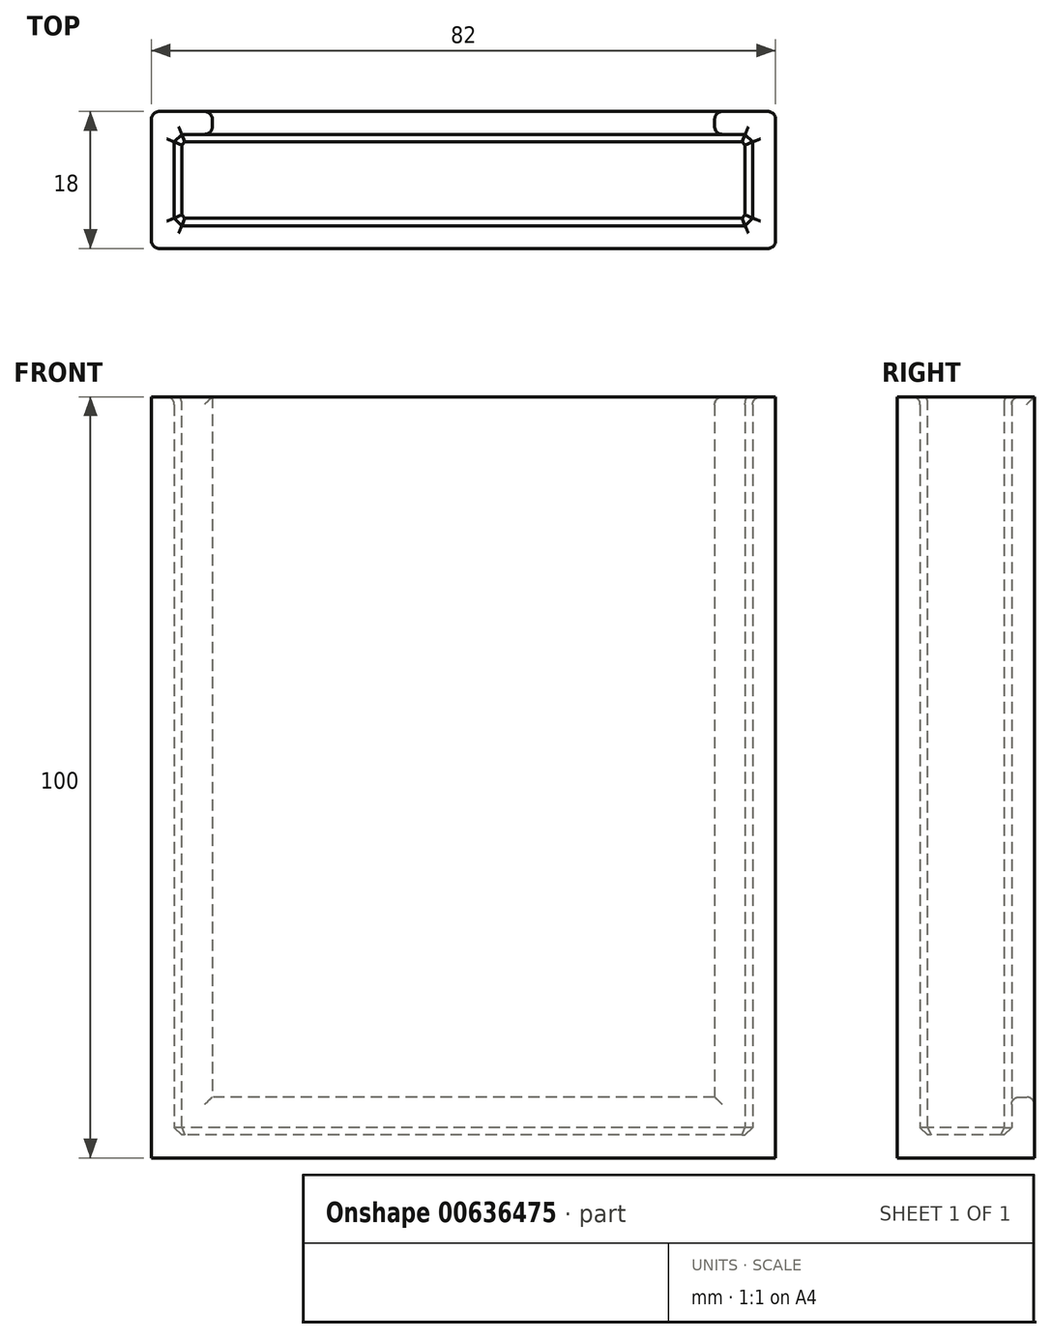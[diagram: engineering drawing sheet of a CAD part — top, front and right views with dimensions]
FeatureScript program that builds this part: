
annotation { "Feature Type Name" : "Feature", "Feature Type Description" : "" }
export const myFeature = defineFeature(function(context is Context, id is Id, definition is map)
    precondition{}
    {
        {
            var Q0;
            Q0=qCreatedBy(makeId("Top.planeOp"),FACE);
            var sketch = newSketch(context, id + "F0", { "sketchPlane" : qUnion([Q0])});
            skLineSegment(sketch, "E0", {"start": v(0, 10.86) * mm, "end": v(-38, 10.86) * mm});
            skLineSegment(sketch, "E1", {"start": v(0, 10.86) * mm, "end": v(38, 10.86) * mm});
            skLineSegment(sketch, "E2", {"start": v(-38, 10.86) * mm, "end": v(-38, 22.86) * mm});
            skLineSegment(sketch, "E3", {"start": v(-38, 22.86) * mm, "end": v(-33, 22.86) * mm});
            skLineSegment(sketch, "E4", {"start": v(-33, 22.86) * mm, "end": v(-33, 25.86) * mm});
            skLineSegment(sketch, "E5", {"start": v(-33, 25.86) * mm, "end": v(-41, 25.86) * mm});
            skLineSegment(sketch, "E6", {"start": v(-41, 25.86) * mm, "end": v(-41, 7.86) * mm});
            skLineSegment(sketch, "E7", {"start": v(-41, 7.86) * mm, "end": v(0, 7.86) * mm});
            skLineSegment(sketch, "E8", {"start": v(0, 7.86) * mm, "end": v(41, 7.86) * mm});
            skLineSegment(sketch, "E9", {"start": v(41, 7.86) * mm, "end": v(41, 25.86) * mm});
            skLineSegment(sketch, "E10", {"start": v(41, 25.86) * mm, "end": v(33, 25.86) * mm});
            skLineSegment(sketch, "E11", {"start": v(33, 25.86) * mm, "end": v(33, 22.86) * mm});
            skLineSegment(sketch, "E12", {"start": v(33, 22.86) * mm, "end": v(38, 22.86) * mm});
            skLineSegment(sketch, "E13", {"start": v(38, 22.86) * mm, "end": v(38, 10.86) * mm});
            skLineSegment(sketch, "E14", {"start": v(41, 25.86) * mm, "end": v(-41, 25.86) * mm});
            skLineSegment(sketch, "E15", {"start": v(33, 22.86) * mm, "end": v(-33, 22.86) * mm});
            skSolve(sketch);
        }
        {
            var Q0;
            Q0=makeQuery(id+"F0.imprint","IMPRINT",FACE,{"disambiguationData":[TD([[makeQuery(id+"F0.imprint","IMPRINT",EDGE,{"derivedFrom":sQuery(id+"F0.wireOp",EDGE,"E0")}),1.0]])]});
            extrude(context, id + "F1", {"entities" : qUnion([Q0]), "depth" : 100 * mm, "offsetDistance" : 25 * mm});
        }
        {
            var Q0;
            Q0=makeQuery(id+"F1.opExtrude","SWEPT_EDGE",EDGE,{"disambiguationData":[OSD([sQuery(id+"F0.wireOp",EDGE,"E9"),sQuery(id+"F0.wireOp",EDGE,"E14")])]});
            var Q1;
            Q1=makeQuery(id+"F1.opExtrude","SWEPT_EDGE",EDGE,{"disambiguationData":[OSD([sQuery(id+"F0.wireOp",EDGE,"E8"),sQuery(id+"F0.wireOp",EDGE,"E9")])]});
            var Q2;
            Q2=makeQuery(id+"F1.opExtrude","SWEPT_EDGE",EDGE,{"disambiguationData":[OSD([sQuery(id+"F0.wireOp",EDGE,"E6"),sQuery(id+"F0.wireOp",EDGE,"E14")])]});
            var Q3;
            Q3=makeQuery(id+"F1.opExtrude","SWEPT_EDGE",EDGE,{"disambiguationData":[OSD([sQuery(id+"F0.wireOp",EDGE,"E6"),sQuery(id+"F0.wireOp",EDGE,"E7")])]});
            fillet(context, id + "F2", {"entities" : qUnion([Q0, Q1, Q2, Q3]), "radius" : 1 * mm, "tangentPropagation" : true, "allowEdgeOverflow" : false});
        }
        {
            var Q0;
            Q0=makeQuery(id+"F1.opExtrude","SWEPT_EDGE",EDGE,{"disambiguationData":[OSD([sQuery(id+"F0.wireOp",EDGE,"E12"),sQuery(id+"F0.wireOp",EDGE,"E13")])]});
            var Q1;
            Q1=makeQuery(id+"F1.opExtrude","SWEPT_EDGE",EDGE,{"disambiguationData":[OSD([sQuery(id+"F0.wireOp",EDGE,"E1"),sQuery(id+"F0.wireOp",EDGE,"E13")])]});
            var Q2;
            Q2=makeQuery(id+"F1.opExtrude","SWEPT_EDGE",EDGE,{"disambiguationData":[OSD([sQuery(id+"F0.wireOp",EDGE,"E0"),sQuery(id+"F0.wireOp",EDGE,"E2")])]});
            var Q3;
            Q3=makeQuery(id+"F1.opExtrude","SWEPT_EDGE",EDGE,{"disambiguationData":[OSD([sQuery(id+"F0.wireOp",EDGE,"E2"),sQuery(id+"F0.wireOp",EDGE,"E3")])]});
            chamfer(context, id + "F3", {"entities" : qUnion([Q0, Q1, Q2, Q3]), "width" : 1 * mm, "tangentPropagation" : true});
        }
        {
            var Q0;
            Q0=makeQuery(id+"F0.imprint","IMPRINT",FACE,{"disambiguationData":[TD([[makeQuery(id+"F0.imprint","IMPRINT",EDGE,{"derivedFrom":sQuery(id+"F0.wireOp",EDGE,"E0")}),-1.0]])]});
            extrude(context, id + "F4", {"entities" : qUnion([Q0]), "operationType" : NewBodyOperationType.ADD, "depth" : 3 * mm, "offsetDistance" : 25 * mm});
        }
        {
            var Q0;
            {var subQ0=sQuery(id+"F0.wireOp",EDGE,"E4");Q0=makeQuery(id+"F0.imprint","IMPRINT",FACE,{"disambiguationData":[TD([[makeQuery(id+"F0.imprint","IMPRINT",EDGE,{"derivedFrom":subQ0}),-1.0]])]});}
            extrude(context, id + "F5", {"entities" : qUnion([Q0]), "operationType" : NewBodyOperationType.ADD, "depth" : 8 * mm, "offsetDistance" : 25 * mm});
        }
        {
            var Q0;
            Q0=makeQuery(id+"F1.opExtrude","CAP_EDGE",EDGE,{"disambiguationData":[OSD([sQuery(id+"F0.wireOp",EDGE,"E0"),sQuery(id+"F0.wireOp",EDGE,"E1")])],"isStart":false});
            var Q1;
            {var subQ0=sQuery(id+"F0.wireOp",EDGE,"E13");var subQ1=sQuery(id+"F0.wireOp",EDGE,"E1");Q1=makeQuery(id+"F3.opChamfer","BLEND_EDGE",EDGE,{"blendedFrom":[makeQuery(id+"F1.opExtrude","SWEPT_EDGE",EDGE,{"disambiguationData":[OSD([subQ1,subQ0])]}),makeQuery(id+"F1.opExtrude","CAP_FACE",FACE,{"disambiguationData":[OSD([sQuery(id+"F0.wireOp",EDGE,"E0"),subQ1,sQuery(id+"F0.wireOp",EDGE,"E2"),sQuery(id+"F0.wireOp",EDGE,"E3"),sQuery(id+"F0.wireOp",EDGE,"E4"),sQuery(id+"F0.wireOp",EDGE,"E6"),sQuery(id+"F0.wireOp",EDGE,"E7"),sQuery(id+"F0.wireOp",EDGE,"E8"),sQuery(id+"F0.wireOp",EDGE,"E9"),sQuery(id+"F0.wireOp",EDGE,"E11"),sQuery(id+"F0.wireOp",EDGE,"E12"),subQ0,sQuery(id+"F0.wireOp",EDGE,"E14")])],"isStart":false})],"blendedInto":[makeQuery(id+"F1.opExtrude","CAP_FACE",FACE,{"disambiguationData":[OSD([sQuery(id+"F0.wireOp",EDGE,"E0"),subQ1,sQuery(id+"F0.wireOp",EDGE,"E2"),sQuery(id+"F0.wireOp",EDGE,"E3"),sQuery(id+"F0.wireOp",EDGE,"E4"),sQuery(id+"F0.wireOp",EDGE,"E6"),sQuery(id+"F0.wireOp",EDGE,"E7"),sQuery(id+"F0.wireOp",EDGE,"E8"),sQuery(id+"F0.wireOp",EDGE,"E9"),sQuery(id+"F0.wireOp",EDGE,"E11"),sQuery(id+"F0.wireOp",EDGE,"E12"),subQ0,sQuery(id+"F0.wireOp",EDGE,"E14")])],"isStart":false})]});}
            var Q2;
            Q2=makeQuery(id+"F1.opExtrude","CAP_EDGE",EDGE,{"disambiguationData":[OSD([sQuery(id+"F0.wireOp",EDGE,"E13")])],"isStart":false});
            var Q3;
            {var subQ0=sQuery(id+"F0.wireOp",EDGE,"E13");var subQ1=sQuery(id+"F0.wireOp",EDGE,"E12");Q3=makeQuery(id+"F3.opChamfer","BLEND_EDGE",EDGE,{"blendedFrom":[makeQuery(id+"F1.opExtrude","SWEPT_EDGE",EDGE,{"disambiguationData":[OSD([subQ1,subQ0])]}),makeQuery(id+"F1.opExtrude","CAP_FACE",FACE,{"disambiguationData":[OSD([sQuery(id+"F0.wireOp",EDGE,"E0"),sQuery(id+"F0.wireOp",EDGE,"E1"),sQuery(id+"F0.wireOp",EDGE,"E2"),sQuery(id+"F0.wireOp",EDGE,"E3"),sQuery(id+"F0.wireOp",EDGE,"E4"),sQuery(id+"F0.wireOp",EDGE,"E6"),sQuery(id+"F0.wireOp",EDGE,"E7"),sQuery(id+"F0.wireOp",EDGE,"E8"),sQuery(id+"F0.wireOp",EDGE,"E9"),sQuery(id+"F0.wireOp",EDGE,"E11"),subQ1,subQ0,sQuery(id+"F0.wireOp",EDGE,"E14")])],"isStart":false})],"blendedInto":[makeQuery(id+"F1.opExtrude","CAP_FACE",FACE,{"disambiguationData":[OSD([sQuery(id+"F0.wireOp",EDGE,"E0"),sQuery(id+"F0.wireOp",EDGE,"E1"),sQuery(id+"F0.wireOp",EDGE,"E2"),sQuery(id+"F0.wireOp",EDGE,"E3"),sQuery(id+"F0.wireOp",EDGE,"E4"),sQuery(id+"F0.wireOp",EDGE,"E6"),sQuery(id+"F0.wireOp",EDGE,"E7"),sQuery(id+"F0.wireOp",EDGE,"E8"),sQuery(id+"F0.wireOp",EDGE,"E9"),sQuery(id+"F0.wireOp",EDGE,"E11"),subQ1,subQ0,sQuery(id+"F0.wireOp",EDGE,"E14")])],"isStart":false})]});}
            var Q4;
            Q4=makeQuery(id+"F1.opExtrude","CAP_EDGE",EDGE,{"disambiguationData":[OSD([sQuery(id+"F0.wireOp",EDGE,"E12")])],"isStart":false});
            fillet(context, id + "F6", {"entities" : qUnion([Q0, Q1, Q2, Q3, Q4]), "radius" : 1 * mm, "tangentPropagation" : true, "allowEdgeOverflow" : false});
        }
        {
            var Q0;
            Q0=makeQuery(id+"F1.opExtrude","SWEPT_EDGE",EDGE,{"disambiguationData":[OSD([sQuery(id+"F0.wireOp",EDGE,"E11"),sQuery(id+"F0.wireOp",EDGE,"E14")])]});
            var Q1;
            Q1=makeQuery(id+"F5.opExtrude","CAP_EDGE",EDGE,{"disambiguationData":[OSD([sQuery(id+"F0.wireOp",EDGE,"E14")])],"isStart":false});
            var Q2;
            Q2=makeQuery(id+"F1.opExtrude","SWEPT_EDGE",EDGE,{"disambiguationData":[OSD([sQuery(id+"F0.wireOp",EDGE,"E4"),sQuery(id+"F0.wireOp",EDGE,"E14")])]});
            var Q3;
            {var subQ0=sQuery(id+"F0.wireOp",EDGE,"E3");var subQ1=sQuery(id+"F0.wireOp",EDGE,"E4");Q3=makeQuery(id+"F4.boolean.opBoolean","SPLIT",EDGE,{"disambiguationData":[topologyDisambiguationEdgeConnected([makeQuery(id+"F1.opExtrude","SWEPT_FACE",FACE,{"disambiguationData":[OSD([subQ0])]})])],"derivedFrom":makeQuery(id+"F1.opExtrude","SWEPT_EDGE",EDGE,{"disambiguationData":[OSD([subQ0,subQ1,sQuery(id+"F0.wireOp",EDGE,"E15")])]})});}
            var Q4;
            Q4=makeQuery(id+"F5.opExtrude","CAP_EDGE",EDGE,{"disambiguationData":[OSD([sQuery(id+"F0.wireOp",EDGE,"E15")])],"isStart":false});
            var Q5;
            {var subQ0=sQuery(id+"F0.wireOp",EDGE,"E11");var subQ1=sQuery(id+"F0.wireOp",EDGE,"E12");Q5=makeQuery(id+"F4.boolean.opBoolean","SPLIT",EDGE,{"disambiguationData":[topologyDisambiguationEdgeConnected([makeQuery(id+"F1.opExtrude","SWEPT_FACE",FACE,{"disambiguationData":[OSD([subQ1])]})])],"derivedFrom":makeQuery(id+"F1.opExtrude","SWEPT_EDGE",EDGE,{"disambiguationData":[OSD([subQ0,subQ1,sQuery(id+"F0.wireOp",EDGE,"E15")])]})});}
            var Q6;
            Q6=makeQuery(id+"F1.opExtrude","CAP_EDGE",EDGE,{"disambiguationData":[OSD([sQuery(id+"F0.wireOp",EDGE,"E2")])],"isStart":false});
            var Q7;
            {var subQ0=sQuery(id+"F0.wireOp",EDGE,"E2");var subQ1=sQuery(id+"F0.wireOp",EDGE,"E0");Q7=makeQuery(id+"F3.opChamfer","BLEND_EDGE",EDGE,{"blendedFrom":[makeQuery(id+"F1.opExtrude","SWEPT_EDGE",EDGE,{"disambiguationData":[OSD([subQ1,subQ0])]}),makeQuery(id+"F1.opExtrude","CAP_FACE",FACE,{"disambiguationData":[OSD([subQ1,sQuery(id+"F0.wireOp",EDGE,"E1"),subQ0,sQuery(id+"F0.wireOp",EDGE,"E3"),sQuery(id+"F0.wireOp",EDGE,"E4"),sQuery(id+"F0.wireOp",EDGE,"E6"),sQuery(id+"F0.wireOp",EDGE,"E7"),sQuery(id+"F0.wireOp",EDGE,"E8"),sQuery(id+"F0.wireOp",EDGE,"E9"),sQuery(id+"F0.wireOp",EDGE,"E11"),sQuery(id+"F0.wireOp",EDGE,"E12"),sQuery(id+"F0.wireOp",EDGE,"E13"),sQuery(id+"F0.wireOp",EDGE,"E14")])],"isStart":false})],"blendedInto":[makeQuery(id+"F1.opExtrude","CAP_FACE",FACE,{"disambiguationData":[OSD([subQ1,sQuery(id+"F0.wireOp",EDGE,"E1"),subQ0,sQuery(id+"F0.wireOp",EDGE,"E3"),sQuery(id+"F0.wireOp",EDGE,"E4"),sQuery(id+"F0.wireOp",EDGE,"E6"),sQuery(id+"F0.wireOp",EDGE,"E7"),sQuery(id+"F0.wireOp",EDGE,"E8"),sQuery(id+"F0.wireOp",EDGE,"E9"),sQuery(id+"F0.wireOp",EDGE,"E11"),sQuery(id+"F0.wireOp",EDGE,"E12"),sQuery(id+"F0.wireOp",EDGE,"E13"),sQuery(id+"F0.wireOp",EDGE,"E14")])],"isStart":false})]});}
            var Q8;
            Q8=makeQuery(id+"F1.opExtrude","CAP_EDGE",EDGE,{"disambiguationData":[OSD([sQuery(id+"F0.wireOp",EDGE,"E3")])],"isStart":false});
            var Q9;
            {var subQ0=sQuery(id+"F0.wireOp",EDGE,"E3");var subQ1=sQuery(id+"F0.wireOp",EDGE,"E2");Q9=makeQuery(id+"F3.opChamfer","BLEND_EDGE",EDGE,{"blendedFrom":[makeQuery(id+"F1.opExtrude","SWEPT_EDGE",EDGE,{"disambiguationData":[OSD([subQ1,subQ0])]}),makeQuery(id+"F1.opExtrude","CAP_FACE",FACE,{"disambiguationData":[OSD([sQuery(id+"F0.wireOp",EDGE,"E0"),sQuery(id+"F0.wireOp",EDGE,"E1"),subQ1,subQ0,sQuery(id+"F0.wireOp",EDGE,"E4"),sQuery(id+"F0.wireOp",EDGE,"E6"),sQuery(id+"F0.wireOp",EDGE,"E7"),sQuery(id+"F0.wireOp",EDGE,"E8"),sQuery(id+"F0.wireOp",EDGE,"E9"),sQuery(id+"F0.wireOp",EDGE,"E11"),sQuery(id+"F0.wireOp",EDGE,"E12"),sQuery(id+"F0.wireOp",EDGE,"E13"),sQuery(id+"F0.wireOp",EDGE,"E14")])],"isStart":false})],"blendedInto":[makeQuery(id+"F1.opExtrude","CAP_FACE",FACE,{"disambiguationData":[OSD([sQuery(id+"F0.wireOp",EDGE,"E0"),sQuery(id+"F0.wireOp",EDGE,"E1"),subQ1,subQ0,sQuery(id+"F0.wireOp",EDGE,"E4"),sQuery(id+"F0.wireOp",EDGE,"E6"),sQuery(id+"F0.wireOp",EDGE,"E7"),sQuery(id+"F0.wireOp",EDGE,"E8"),sQuery(id+"F0.wireOp",EDGE,"E9"),sQuery(id+"F0.wireOp",EDGE,"E11"),sQuery(id+"F0.wireOp",EDGE,"E12"),sQuery(id+"F0.wireOp",EDGE,"E13"),sQuery(id+"F0.wireOp",EDGE,"E14")])],"isStart":false})]});}
            var Q10;
            {var subQ0=sQuery(id+"F0.wireOp",EDGE,"E14");Q10=makeQuery(id+"F1.opExtrude","CAP_EDGE",EDGE,{"disambiguationData":[OSD([subQ0]),TDD([makeQuery(id+"F0.imprint","IMPRINT",EDGE,{"disambiguationData":[TD([[makeQuery(id+"F0.imprint","INTERSECT",VERTEX,{"derivedFrom":[sQuery(id+"F0.wireOp",EDGE,"E4"),subQ0]}),-1.0]])],"derivedFrom":subQ0})])],"isStart":false});}
            fillet(context, id + "F7", {"entities" : qUnion([Q0, Q1, Q2, Q3, Q4, Q5, Q6, Q7, Q8, Q9, Q10]), "radius" : 1 * mm, "tangentPropagation" : true, "allowEdgeOverflow" : false});
        }
        {
            var Q0;
            Q0=makeQuery(id+"F4.opExtrude","CAP_FACE",FACE,{"disambiguationData":[OSD([sQuery(id+"F0.wireOp",EDGE,"E0"),sQuery(id+"F0.wireOp",EDGE,"E1"),sQuery(id+"F0.wireOp",EDGE,"E2"),sQuery(id+"F0.wireOp",EDGE,"E3"),sQuery(id+"F0.wireOp",EDGE,"E12"),sQuery(id+"F0.wireOp",EDGE,"E13"),sQuery(id+"F0.wireOp",EDGE,"E15")])],"isStart":false});
            chamfer(context, id + "F8", {"entities" : qUnion([Q0]), "width" : 1 * mm, "tangentPropagation" : true});
        }
    });
